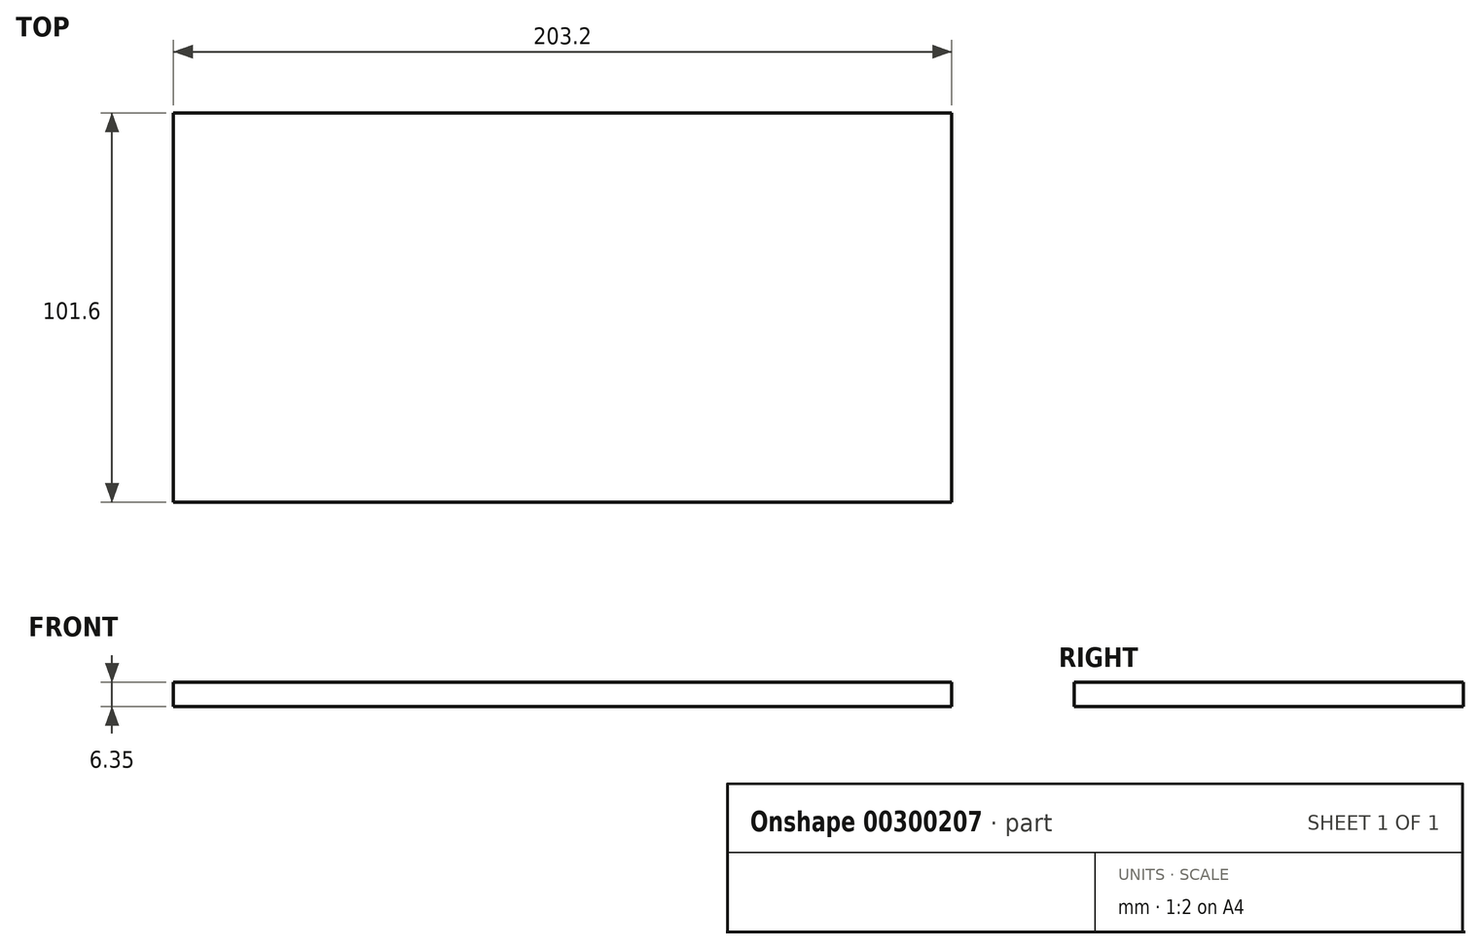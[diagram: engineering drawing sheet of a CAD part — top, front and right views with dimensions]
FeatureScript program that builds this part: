
annotation { "Feature Type Name" : "Feature", "Feature Type Description" : "" }
export const myFeature = defineFeature(function(context is Context, id is Id, definition is map)
    precondition{}
    {
        {
            var Q0;
            Q0=qCreatedBy(makeId("Top.planeOp"),FACE);
            var sketch = newSketch(context, id + "F0", { "sketchPlane" : qUnion([Q0])});
            skLineSegment(sketch, "E0.bottom", {"start": v(-91.02, -62.75) * mm, "end": v(112.18, -62.75) * mm});
            skLineSegment(sketch, "E0.top", {"start": v(-91.02, 38.85) * mm, "end": v(112.18, 38.85) * mm});
            skLineSegment(sketch, "E0.left", {"start": v(-91.02, -62.75) * mm, "end": v(-91.02, 38.85) * mm});
            skLineSegment(sketch, "E0.right", {"start": v(112.18, -62.75) * mm, "end": v(112.18, 38.85) * mm});
            skSolve(sketch);
        }
        {
            var Q0;
            Q0=makeQuery(id+"F0.imprint","IMPRINT",FACE,{"disambiguationData":[TD([[makeQuery(id+"F0.imprint","IMPRINT",EDGE,{"derivedFrom":sQuery(id+"F0.wireOp",EDGE,"E0.bottom")}),1.0]])]});
            extrude(context, id + "F1", {"entities" : qUnion([Q0]), "depth" : 6.35 * mm});
        }
    });
